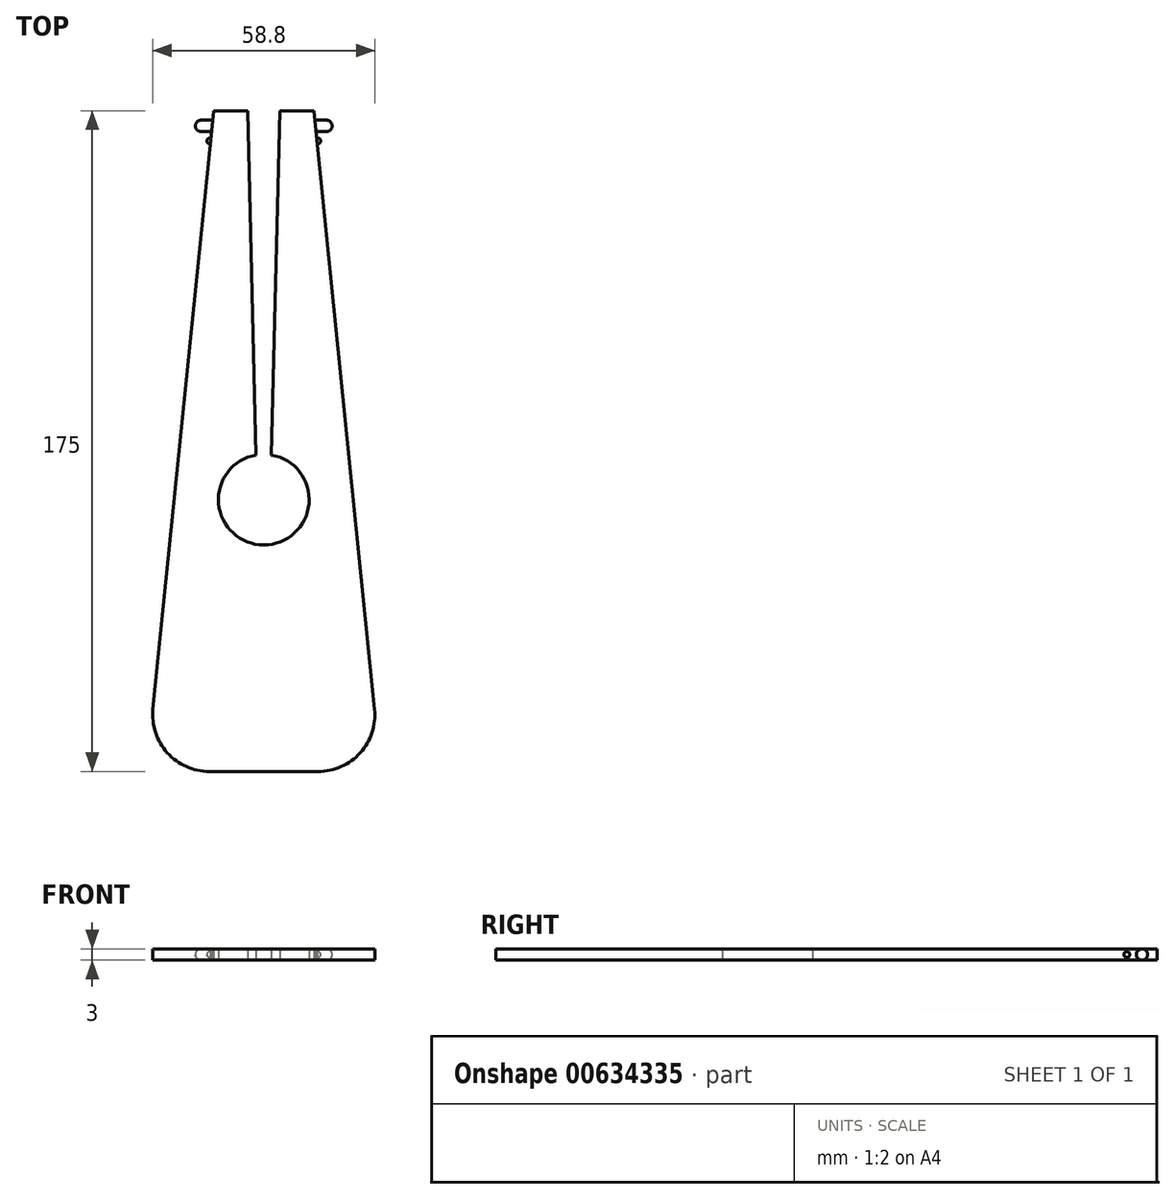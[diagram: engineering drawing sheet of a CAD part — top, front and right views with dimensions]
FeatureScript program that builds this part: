
annotation { "Feature Type Name" : "Feature", "Feature Type Description" : "" }
export const myFeature = defineFeature(function(context is Context, id is Id, definition is map)
    precondition{}
    {
        {
            var Q0;
            Q0=qCreatedBy(makeId("Top.planeOp"),FACE);
            var sketch = newSketch(context, id + "F0", { "sketchPlane" : qUnion([Q0])});
            skLineSegment(sketch, "E0", {"start": v(0, 0) * mm, "end": v(14.4, 0) * mm});
            skLineSegment(sketch, "E1", {"start": v(0, 0) * mm, "end": v(0, 175) * mm, "construction": true});
            skLineSegment(sketch, "E2", {"start": v(0, 175) * mm, "end": v(4.25, 175) * mm, "construction": true});
            skLineSegment(sketch, "E3", {"start": v(13.25, 175) * mm, "end": v(29.33, 16.51) * mm});
            skPoint(sketch, "E4", {"position": v(0, 60) * mm});
            skPoint(sketch, "E5", {"position": v(0, 72) * mm});
            skArc(sketch, "E6", {"start": v(0, 60) * mm, "mid": v(11.96, 70.98) * mm, "end": v(2.04, 83.83) * mm});
            skLineSegment(sketch, "E7", {"start": v(4.25, 175) * mm, "end": v(2.04, 83.83) * mm});
            skLineSegment(sketch, "E8", {"start": v(4.25, 175) * mm, "end": v(13.25, 175) * mm});
            skLineSegment(sketch, "E9.MirrorCS", {"start": v(-4.25, 175) * mm, "end": v(-2.04, 83.83) * mm});
            skLineSegment(sketch, "E10.MirrorCS", {"start": v(-13.25, 175) * mm, "end": v(-29.33, 16.51) * mm});
            skArc(sketch, "E11.MirrorCS", {"start": v(0, 60) * mm, "mid": v(-11.96, 70.98) * mm, "end": v(-2.04, 83.83) * mm});
            skLineSegment(sketch, "E12.MirrorCS", {"start": v(0, 0) * mm, "end": v(-14.4, 0) * mm});
            skLineSegment(sketch, "E13.MirrorCS", {"start": v(0, 175) * mm, "end": v(-13.25, 175) * mm, "construction": true});
            skLineSegment(sketch, "E14.MirrorCS", {"start": v(-4.25, 175) * mm, "end": v(-13.25, 175) * mm});
            skPoint(sketch, "E15", {"position": v(15.5, 0) * mm});
            skLineSegment(sketch, "E16", {"start": v(0, 60) * mm, "end": v(34.32, 60) * mm, "construction": true});
            skLineSegment(sketch, "E17", {"start": v(34.32, 60) * mm, "end": v(24.91, 60) * mm, "construction": true});
            skPoint(sketch, "E18", {"position": v(29.46, 15.23) * mm});
            skPoint(sketch, "E19.visualSharp", {"position": v(31, 0) * mm});
            skArc(sketch, "E19.filletArc", {"start": v(14.4, 0) * mm, "mid": v(25.53, 4.94) * mm, "end": v(29.33, 16.51) * mm});
            skArc(sketch, "E20.MirrorCS", {"start": v(-14.4, 0) * mm, "mid": v(-25.53, 4.94) * mm, "end": v(-29.33, 16.51) * mm});
            skPoint(sketch, "E21.orphan", {"position": v(-31, 0) * mm});
            skSolve(sketch);
        }
        {
            var Q0;
            Q0 = qSketchRegion(id + "F0", true);
            extrude(context, id + "F1", {"entities" : qUnion([Q0]), "depth" : 3 * mm, "offsetDistance" : 25 * mm});
        }
        {
            var Q0;
            Q0=qCreatedBy(makeId("Right.planeOp"),FACE);
            cPlane(context, id + "F2", {"entities" : qUnion([Q0]), "cplaneType" : CPlaneType.OFFSET, "offset" : 13.25 * mm, "width" : 150 * mm, "height" : 150 * mm});
        }
        {
            var Q0;
            Q0=qCreatedBy(id+"F2.planeOp",FACE);
            var sketch = newSketch(context, id + "F3", { "sketchPlane" : qUnion([Q0])});
            skLineSegment(sketch, "E22", {"start": v(0, 0) * mm, "end": v(175.25, 0) * mm});
            skLineSegment(sketch, "E23", {"start": v(175.25, 0) * mm, "end": v(171, 0) * mm, "construction": true});
            skLineSegment(sketch, "E24", {"start": v(171, 0) * mm, "end": v(171, 1.5) * mm, "construction": true});
            skCircle(sketch, "E25", {"center": v(171, 1.5) * mm, "radius": 1.5 * mm});
            skLineSegment(sketch, "E26", {"start": v(171, 1.5) * mm, "end": v(167, 1.5) * mm, "construction": true});
            skCircle(sketch, "E27", {"center": v(167, 1.5) * mm, "radius": 0.78 * mm});
            skSolve(sketch);
        }
        {
            var Q0;
            Q0=makeQuery(id+"F3.imprint","IMPRINT",FACE,{"disambiguationData":[TD([[makeQuery(id+"F3.imprint","IMPRINT",EDGE,{"derivedFrom":sQuery(id+"F3.wireOp",EDGE,"E25")}),1.0]])]});
            extrude(context, id + "F4", {"entities" : qUnion([Q0]), "depth" : 4.85 * mm, "offsetDistance" : 25 * mm});
        }
        {
            var Q0;
            Q0=makeQuery(id+"F3.imprint","IMPRINT",FACE,{"disambiguationData":[TD([[makeQuery(id+"F3.imprint","IMPRINT",EDGE,{"derivedFrom":sQuery(id+"F3.wireOp",EDGE,"E27")}),1.0]])]});
            extrude(context, id + "F5", {"entities" : qUnion([Q0]), "depth" : 1.8 * mm, "offsetDistance" : 25 * mm});
        }
        {
            var Q0;
            Q0=makeQuery(id+"F4.opExtrude","CAP_FACE",FACE,{"disambiguationData":[OSD([sQuery(id+"F3.wireOp",EDGE,"E25")])],"isStart":false});
            fillet(context, id + "F6", {"entities" : qUnion([Q0]), "radius" : 1.5 * mm, "tangentPropagation" : true, "allowEdgeOverflow" : false});
        }
        {
            var Q0;
            Q0=makeQuery(id+"F5.opExtrude","CAP_FACE",FACE,{"disambiguationData":[OSD([sQuery(id+"F3.wireOp",EDGE,"E27")])],"isStart":false});
            fillet(context, id + "F7", {"entities" : qUnion([Q0]), "radius" : 1.55 / 2 * mm, "tangentPropagation" : true, "allowEdgeOverflow" : false});
        }
        {
            var Q0;
            Q0=makeQuery(id+"F4.opExtrude","SWEPT_BODY",BODY,{"disambiguationData":[OSD([sQuery(id+"F3.wireOp",EDGE,"E25")])]});
            var Q1;
            Q1=makeQuery(id+"F5.opExtrude","SWEPT_BODY",BODY,{"disambiguationData":[OSD([sQuery(id+"F3.wireOp",EDGE,"E27")])]});
            var Q2;
            Q2=qCreatedBy(makeId("Right.planeOp"),FACE);
            mirror(context, id + "F8", {"operationType" : NewBodyOperationType.ADD, "entities" : qUnion([Q0, Q1]), "mirrorPlane" : qUnion([Q2])});
        }
    });
